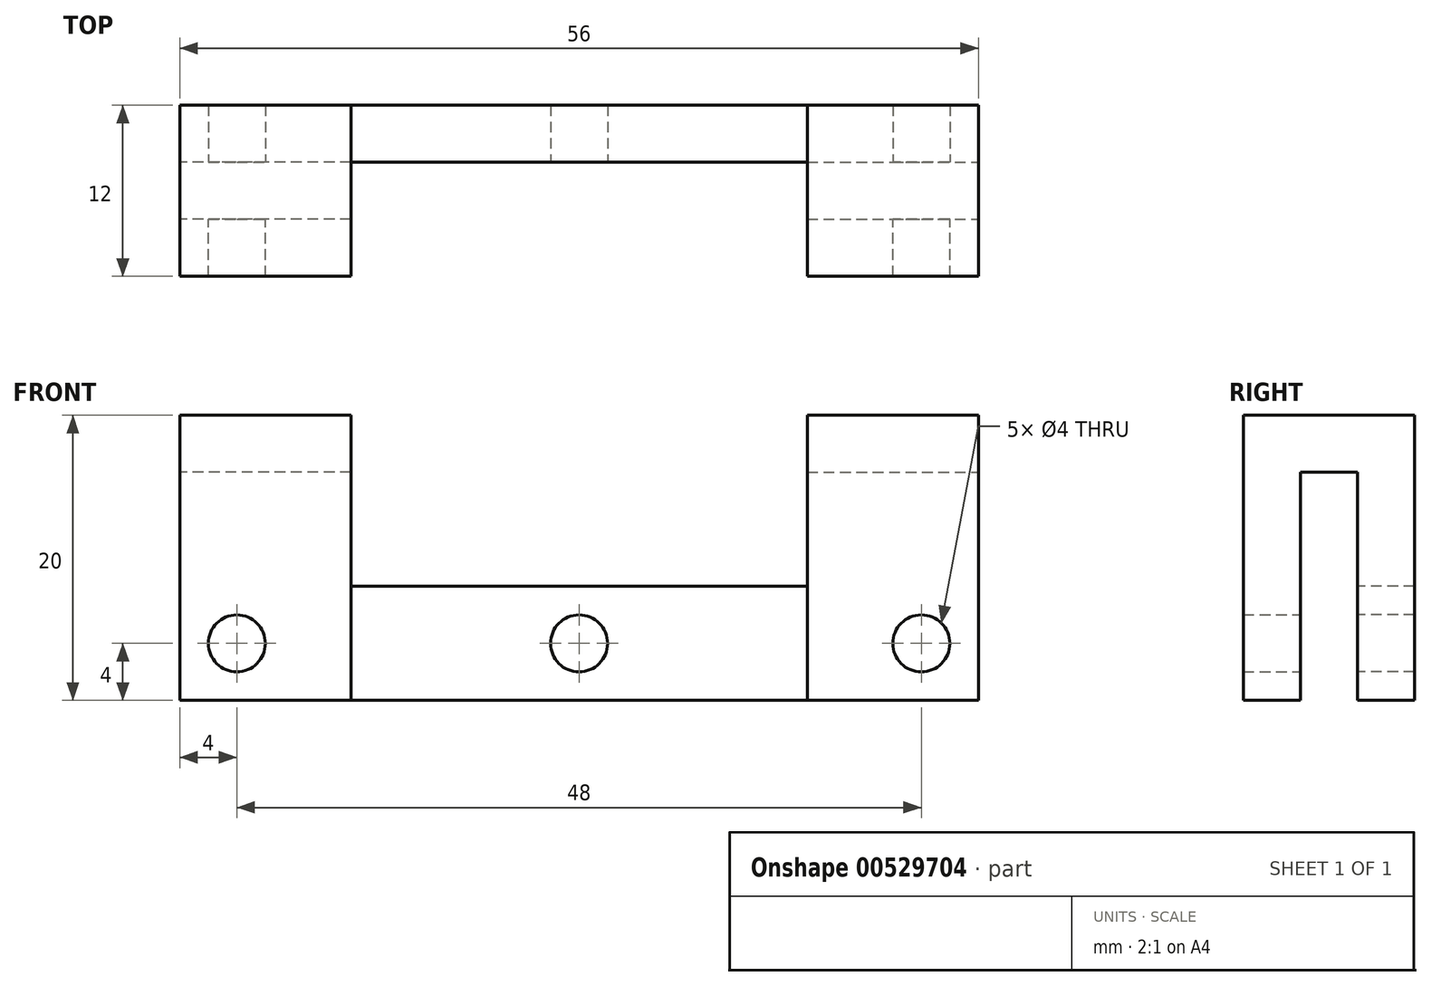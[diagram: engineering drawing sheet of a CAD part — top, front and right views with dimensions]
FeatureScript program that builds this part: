
annotation { "Feature Type Name" : "Feature", "Feature Type Description" : "" }
export const myFeature = defineFeature(function(context is Context, id is Id, definition is map)
    precondition{}
    {
        {
            var Q0;
            Q0=qCreatedBy(makeId("Front.planeOp"),FACE);
            var sketch = newSketch(context, id + "F0", { "sketchPlane" : qUnion([Q0])});
            skLineSegment(sketch, "E0.bottom", {"start": v(28, -4) * mm, "end": v(-28, -4) * mm});
            skLineSegment(sketch, "E0.top", {"start": v(16, 4) * mm, "end": v(-16, 4) * mm});
            skLineSegment(sketch, "E0.left", {"start": v(28, -4) * mm, "end": v(28, 4) * mm});
            skLineSegment(sketch, "E0.right", {"start": v(-28, -4) * mm, "end": v(-28, 4) * mm});
            skPoint(sketch, "E0.middle", {"position": v(0, 0) * mm});
            skCircle(sketch, "E1", {"center": v(-24, 0) * mm, "radius": 2 * mm});
            skCircle(sketch, "E2.MirrorC", {"center": v(24, 0) * mm, "radius": 2 * mm});
            skLineSegment(sketch, "E3.top", {"start": v(28, 16) * mm, "end": v(16, 16) * mm});
            skLineSegment(sketch, "E3.left", {"start": v(28, 4) * mm, "end": v(28, 16) * mm});
            skLineSegment(sketch, "E3.right", {"start": v(16, 4) * mm, "end": v(16, 16) * mm});
            skLineSegment(sketch, "E4.MirrorCS", {"start": v(-28, 4) * mm, "end": v(-28, 16) * mm});
            skLineSegment(sketch, "E5.MirrorCS", {"start": v(-16, 4) * mm, "end": v(-16, 16) * mm});
            skLineSegment(sketch, "E6.MirrorCS", {"start": v(-28, 16) * mm, "end": v(-16, 16) * mm});
            skCircle(sketch, "E7", {"center": v(0, 0) * mm, "radius": 2 * mm});
            skSolve(sketch);
        }
        {
            var Q0;
            Q0=qSketchRegion(id+"F0",true);
            extrude(context, id + "F1", {"entities" : qUnion([Q0]), "oppositeDirection" : true, "depth" : 4 * mm, "offsetDistance" : 25 * mm});
        }
        {
            var Q0;
            Q0=makeQuery(id+"F1.opExtrude","CAP_FACE",FACE,{"disambiguationData":[OSD([sQuery(id+"F0.wireOp",EDGE,"E0.bottom"),sQuery(id+"F0.wireOp",EDGE,"E0.top"),sQuery(id+"F0.wireOp",EDGE,"E0.left"),sQuery(id+"F0.wireOp",EDGE,"E0.right"),sQuery(id+"F0.wireOp",EDGE,"E1"),sQuery(id+"F0.wireOp",EDGE,"E2.MirrorC"),sQuery(id+"F0.wireOp",EDGE,"E3.top"),sQuery(id+"F0.wireOp",EDGE,"E3.left"),sQuery(id+"F0.wireOp",EDGE,"E3.right"),sQuery(id+"F0.wireOp",EDGE,"E4.MirrorCS"),sQuery(id+"F0.wireOp",EDGE,"E5.MirrorCS"),sQuery(id+"F0.wireOp",EDGE,"E6.MirrorCS")])],"isStart":true});
            var sketch = newSketch(context, id + "F2", { "sketchPlane" : qUnion([Q0])});
            skLineSegment(sketch, "E8.bottom", {"start": v(16, 16) * mm, "end": v(28, 16) * mm});
            skLineSegment(sketch, "E8.top", {"start": v(16, 12) * mm, "end": v(28, 12) * mm});
            skLineSegment(sketch, "E8.left", {"start": v(28, 16) * mm, "end": v(28, 12) * mm});
            skLineSegment(sketch, "E8.right", {"start": v(16, 16) * mm, "end": v(16, 12) * mm});
            skLineSegment(sketch, "E9.MirrorCS", {"start": v(-16, 16) * mm, "end": v(-16, 12) * mm});
            skLineSegment(sketch, "E10.MirrorCS", {"start": v(-28, 16) * mm, "end": v(-28, 12) * mm});
            skLineSegment(sketch, "E11.MirrorCS", {"start": v(-16, 12) * mm, "end": v(-28, 12) * mm});
            skLineSegment(sketch, "E12.MirrorCS", {"start": v(-16, 16) * mm, "end": v(-28, 16) * mm});
            skSolve(sketch);
        }
        {
            var Q0;
            Q0=qSketchRegion(id+"F2",true);
            extrude(context, id + "F3", {"entities" : qUnion([Q0]), "operationType" : NewBodyOperationType.ADD, "depth" : 4 * mm, "offsetDistance" : 25 * mm});
        }
        {
            var Q0;
            Q0=makeQuery(id+"F3.opExtrude","CAP_FACE",FACE,{"disambiguationData":[OSD([sQuery(id+"F2.wireOp",EDGE,"E8.bottom"),sQuery(id+"F2.wireOp",EDGE,"E8.top"),sQuery(id+"F2.wireOp",EDGE,"E8.left"),sQuery(id+"F2.wireOp",EDGE,"E8.right")])],"isStart":false});
            var sketch = newSketch(context, id + "F4", { "sketchPlane" : qUnion([Q0])});
            skCircle(sketch, "E13", {"center": v(24, 0) * mm, "radius": 2 * mm});
            skLineSegment(sketch, "E14.bottom", {"start": v(28, 16) * mm, "end": v(16, 16) * mm});
            skLineSegment(sketch, "E14.top", {"start": v(28, -4) * mm, "end": v(16, -4) * mm});
            skLineSegment(sketch, "E14.left", {"start": v(16, 16) * mm, "end": v(16, -4) * mm});
            skLineSegment(sketch, "E14.right", {"start": v(28, 16) * mm, "end": v(28, -4) * mm});
            skLineSegment(sketch, "E15.MirrorCS", {"start": v(-16, 16) * mm, "end": v(-16, -4) * mm});
            skLineSegment(sketch, "E16.MirrorCS", {"start": v(-28, 16) * mm, "end": v(-16, 16) * mm});
            skCircle(sketch, "E17.MirrorC", {"center": v(-24, 0) * mm, "radius": 2 * mm});
            skLineSegment(sketch, "E18.MirrorCS", {"start": v(-28, 16) * mm, "end": v(-28, -4) * mm});
            skLineSegment(sketch, "E19.MirrorCS", {"start": v(-28, -4) * mm, "end": v(-16, -4) * mm});
            skSolve(sketch);
        }
        {
            var Q0;
            Q0=qSketchRegion(id+"F4",true);
            extrude(context, id + "F5", {"entities" : qUnion([Q0]), "operationType" : NewBodyOperationType.ADD, "depth" : 4 * mm, "offsetDistance" : 25 * mm});
        }
    });
